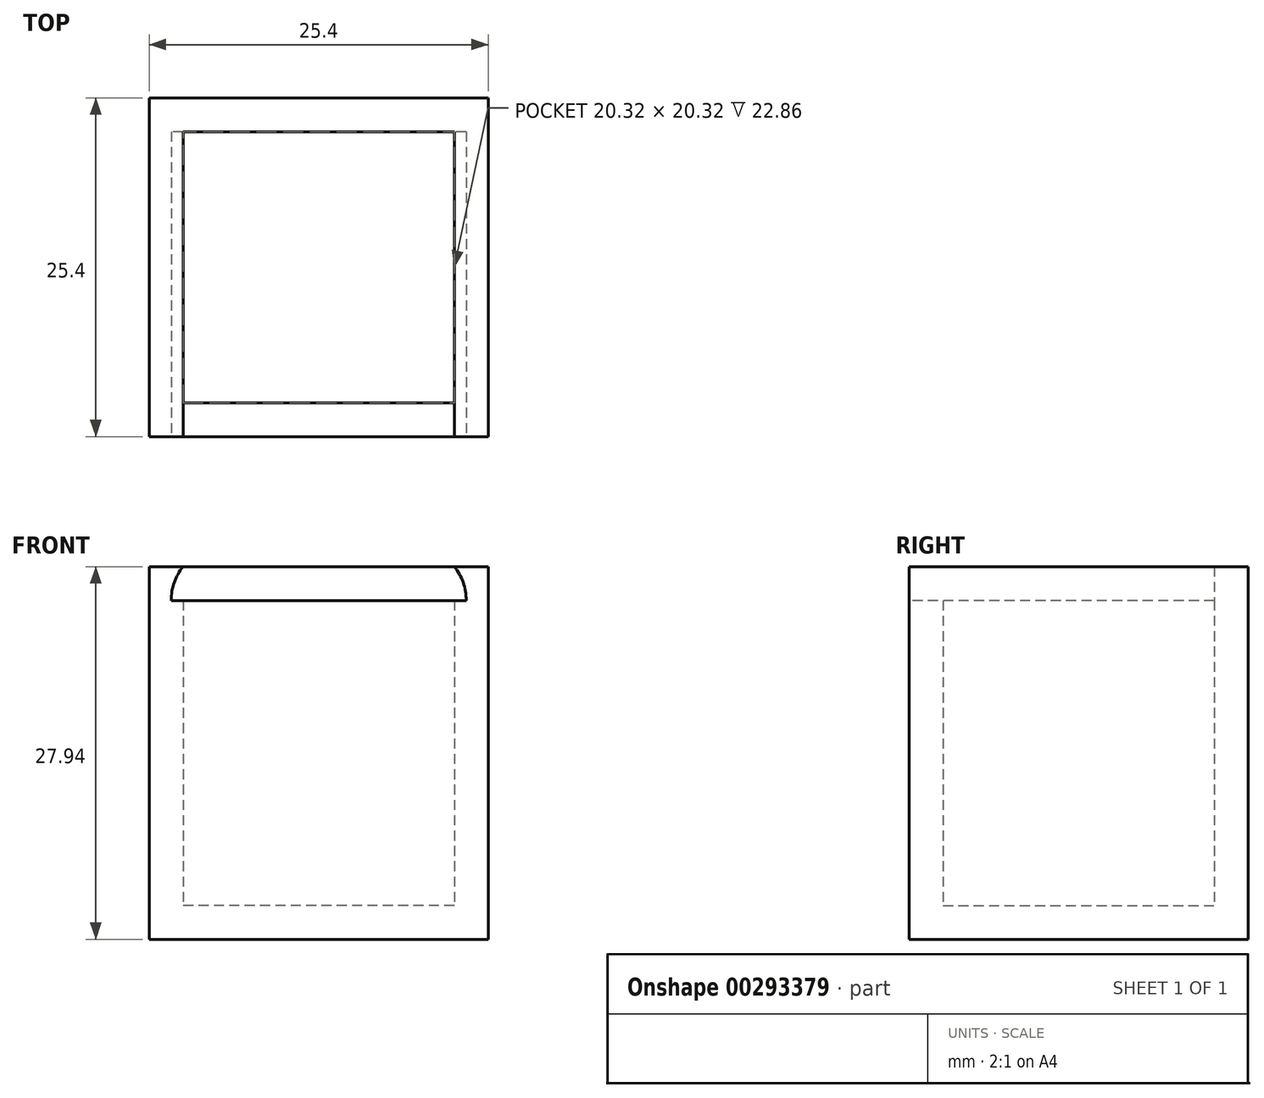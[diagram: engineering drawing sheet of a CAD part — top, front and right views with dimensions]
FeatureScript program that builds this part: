
annotation { "Feature Type Name" : "Feature", "Feature Type Description" : "" }
export const myFeature = defineFeature(function(context is Context, id is Id, definition is map)
    precondition{}
    {
        {
            var Q0;
            Q0=qCreatedBy(makeId("Front.planeOp"),FACE);
            var sketch = newSketch(context, id + "F0", { "sketchPlane" : qUnion([Q0])});
            skLineSegment(sketch, "E0.bottom", {"start": v(12.7, 13.97) * mm, "end": v(-12.7, 13.97) * mm});
            skLineSegment(sketch, "E0.top", {"start": v(12.7, -13.97) * mm, "end": v(-12.7, -13.97) * mm});
            skLineSegment(sketch, "E0.left", {"start": v(12.7, 13.97) * mm, "end": v(12.7, -13.97) * mm});
            skLineSegment(sketch, "E0.right", {"start": v(-12.7, 13.97) * mm, "end": v(-12.7, -13.97) * mm});
            skPoint(sketch, "E0.middle", {"position": v(0, 0) * mm});
            skSolve(sketch);
        }
        {
            var Q0;
            Q0=makeQuery(id+"F0.imprint","IMPRINT",FACE,{"disambiguationData":[TD([[makeQuery(id+"F0.imprint","IMPRINT",EDGE,{"derivedFrom":sQuery(id+"F0.wireOp",EDGE,"E0.bottom")}),1.0]])]});
            extrude(context, id + "F1", {"entities" : qUnion([Q0]), "depth" : 25.4 * mm});
        }
        {
            var Q0;
            Q0=makeQuery(id+"F1.opExtrude","SWEPT_FACE",FACE,{"disambiguationData":[OSD([sQuery(id+"F0.wireOp",EDGE,"E0.bottom")])]});
            shell(context, id + "F2", {"entities" : qUnion([Q0]), "thickness" : 2.54 * mm});
        }
        {
            var Q0;
            Q0=makeQuery(id+"F1.opExtrude","CAP_FACE",FACE,{"disambiguationData":[OSD([sQuery(id+"F0.wireOp",EDGE,"E0.bottom"),sQuery(id+"F0.wireOp",EDGE,"E0.top"),sQuery(id+"F0.wireOp",EDGE,"E0.left"),sQuery(id+"F0.wireOp",EDGE,"E0.right")])],"isStart":false});
            var sketch = newSketch(context, id + "F3", { "sketchPlane" : qUnion([Q0])});
            skLineSegment(sketch, "E1", {"start": v(11.06, 11.43) * mm, "end": v(-11.05, 11.43) * mm});
            skLineSegment(sketch, "E2", {"start": v(-10.16, 13.97) * mm, "end": v(10.16, 13.97) * mm});
            skArc(sketch, "E3", {"start": v(-10.16, 13.97) * mm, "mid": v(-10.82, 12.78) * mm, "end": v(-11.05, 11.43) * mm});
            skArc(sketch, "E4", {"start": v(11.06, 11.43) * mm, "mid": v(10.83, 12.78) * mm, "end": v(10.16, 13.97) * mm});
            skSolve(sketch);
        }
        {
            var Q0;
            Q0=makeQuery(id+"F3.imprint","IMPRINT",FACE,{"disambiguationData":[TD([[makeQuery(id+"F3.imprint","IMPRINT",EDGE,{"derivedFrom":sQuery(id+"F3.wireOp",EDGE,"E1")}),-1.0]])]});
            extrude(context, id + "F4", {"entities" : qUnion([Q0]), "operationType" : NewBodyOperationType.REMOVE, "oppositeDirection" : true, "depth" : 22.86 * mm});
        }
    });
